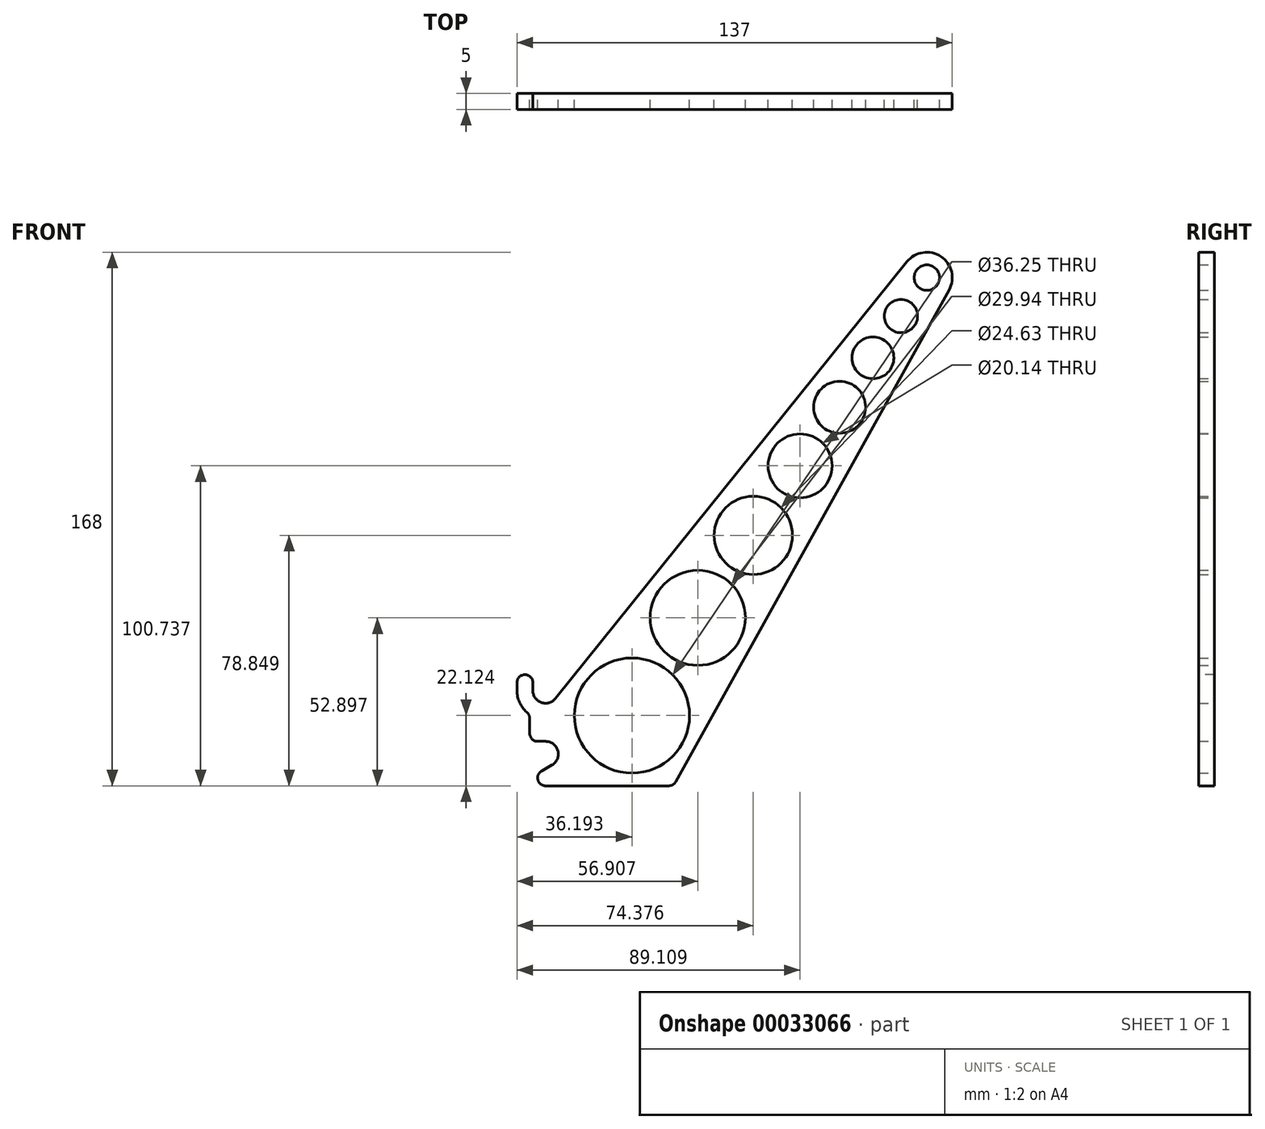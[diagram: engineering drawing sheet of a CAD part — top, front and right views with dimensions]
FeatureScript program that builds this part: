
annotation { "Feature Type Name" : "Feature", "Feature Type Description" : "" }
export const myFeature = defineFeature(function(context is Context, id is Id, definition is map)
    precondition{}
    {
        {
            var Q0;
            Q0=qCreatedBy(makeId("Front.planeOp"),FACE);
            var sketch = newSketch(context, id + "F0", { "sketchPlane" : qUnion([Q0])});
            skCircle(sketch, "E0", {"center": v(0, 0) * mm, "radius": 4 * mm});
            skCircle(sketch, "E1", {"center": v(0, -20) * mm, "radius": 4 * mm});
            skCircle(sketch, "E2", {"center": v(120, 130) * mm, "radius": 4 * mm});
            skLineSegment(sketch, "E3", {"start": v(113.77, 135.02) * mm, "end": v(3.12, -2.5) * mm});
            skLineSegment(sketch, "E4", {"start": v(127, 126.11) * mm, "end": v(40.2, -30) * mm});
            skArc(sketch, "E5", {"start": v(127, 126.11) * mm, "mid": v(124.47, 136.64) * mm, "end": v(113.77, 135.02) * mm});
            skLineSegment(sketch, "E6", {"start": v(-4, 0) * mm, "end": v(-4, 5) * mm});
            skLineSegment(sketch, "E7", {"start": v(-9, 5) * mm, "end": v(-9, 0) * mm});
            skArc(sketch, "E8", {"start": v(-9, 0) * mm, "mid": v(-7.94, -4.24) * mm, "end": v(-5, -7.48) * mm});
            skLineSegment(sketch, "E9", {"start": v(0, -16) * mm, "end": v(-5, -16) * mm});
            skLineSegment(sketch, "E10", {"start": v(-5, -16) * mm, "end": v(-5, -7.48) * mm});
            skPoint(sketch, "E11.orphan", {"position": v(0, -9) * mm});
            skLineSegment(sketch, "E12", {"start": v(-9, 5) * mm, "end": v(-4, 5) * mm});
            skLineSegment(sketch, "E13", {"start": v(-9.32, -30) * mm, "end": v(40.2, -30) * mm});
            skCircle(sketch, "E14", {"center": v(27.2, -7.88) * mm, "radius": 18.12 * mm});
            skCircle(sketch, "E15", {"center": v(47.9, 22.9) * mm, "radius": 14.97 * mm});
            skCircle(sketch, "E16", {"center": v(65.38, 48.85) * mm, "radius": 12.31 * mm});
            skCircle(sketch, "E17", {"center": v(80.1, 70.74) * mm, "radius": 10.07 * mm});
            skCircle(sketch, "E18", {"center": v(92.53, 89.2) * mm, "radius": 8.18 * mm});
            skCircle(sketch, "E19", {"center": v(103.01, 104.76) * mm, "radius": 6.59 * mm});
            skCircle(sketch, "E20", {"center": v(111.85, 117.9) * mm, "radius": 5.24 * mm});
            skLineSegment(sketch, "E21", {"start": v(2, -23.46) * mm, "end": v(-9.32, -30) * mm});
            skSolve(sketch);
        }
        {
            var Q0;
            Q0=makeQuery(id+"F0.imprint","IMPRINT",FACE,{"disambiguationData":[TD([[makeQuery(id+"F0.imprint","IMPRINT",EDGE,{"derivedFrom":sQuery(id+"F0.wireOp",EDGE,"E2")}),-1.0]])]});
            extrude(context, id + "F1", {"entities" : qUnion([Q0]), "depth" : 5 * mm});
        }
        {
            var Q0;
            Q0=makeQuery(id+"F1.opExtrude","SWEPT_EDGE",EDGE,{"disambiguationData":[OSD([sQuery(id+"F0.wireOp",EDGE,"E7"),sQuery(id+"F0.wireOp",EDGE,"E12")])]});
            var Q1;
            Q1=makeQuery(id+"F1.opExtrude","SWEPT_EDGE",EDGE,{"disambiguationData":[OSD([sQuery(id+"F0.wireOp",EDGE,"E6"),sQuery(id+"F0.wireOp",EDGE,"E12")])]});
            var Q2;
            Q2=makeQuery(id+"F1.opExtrude","SWEPT_EDGE",EDGE,{"disambiguationData":[OSD([sQuery(id+"F0.wireOp",EDGE,"E13"),sQuery(id+"F0.wireOp",EDGE,"E21")])]});
            var Q3;
            Q3=makeQuery(id+"F1.opExtrude","SWEPT_EDGE",EDGE,{"disambiguationData":[OSD([sQuery(id+"F0.wireOp",EDGE,"E4"),sQuery(id+"F0.wireOp",EDGE,"E13")])]});
            var Q4;
            Q4=makeQuery(id+"F1.opExtrude","SWEPT_EDGE",EDGE,{"disambiguationData":[OSD([sQuery(id+"F0.wireOp",EDGE,"E8"),sQuery(id+"F0.wireOp",EDGE,"E10")])]});
            var Q5;
            Q5=makeQuery(id+"F1.opExtrude","SWEPT_EDGE",EDGE,{"disambiguationData":[OSD([sQuery(id+"F0.wireOp",EDGE,"E9"),sQuery(id+"F0.wireOp",EDGE,"E10")])]});
            fillet(context, id + "F2", {"entities" : qUnion([Q0, Q1, Q2, Q3, Q4, Q5]), "radius" : 2.5 * mm, "tangentPropagation" : true, "allowEdgeOverflow" : false});
        }
    });
